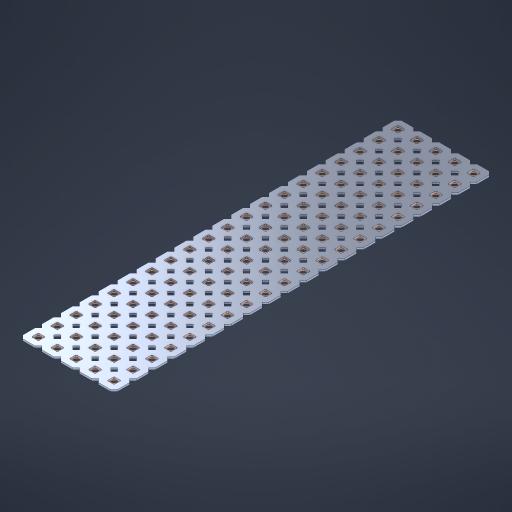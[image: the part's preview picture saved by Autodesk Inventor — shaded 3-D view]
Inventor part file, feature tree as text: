
AUTODESK INVENTOR PART (.ipt)
format: ipt  version: 2023 (Build 270158000, 158)  size: 1,413,120 bytes
history: native  units: in
note: dims shown in document units (in); Inventor stores cm internally (conversion verified against a paired STEP export)
features: other x101, extrude x99, sketch x2, pattern_linear x1
ambient origin geometry x8: Origin, YZ Plane, XZ Plane, XY Plane, X Axis, Y Axis, Z Axis, Center Point
bodies: Solid1 (feature_tree), Body (feature_tree)
feature tree (203):
  pattern_linear  "Rectangular Pattern1"  Spacing1=0.09in  [1 undecoded]
  sketch  "Sketch1"  dims[d1=0.5in]
  sketch  "Sketch2"  dims[d2=0.182in d3=0.09in d4=0.09in d5=0.09in d6=0.09in d7=0.09in d8=0.09in d9=0.09in d10=0.09in d11=0.02in d13=0.0in d14=0.172in d15=0.0625in d16=0.0in d19=0.5in d22=0.5in]
  other  "Srf1"
  other  "Srf126"
  other  "Srf127"
  other  "Srf128"
  other  "Srf129"
  other  "Srf130"
  other  "Srf131"
  other  "Srf250"
  other  "Srf251"
  other  "Srf252"
  other  "Srf253"
  other  "Srf254"
  other  "Srf255"
  other  "Srf256"
  other  "Srf257"
  other  "Srf258"
  other  "Srf259"
  other  "Srf260"
  other  "Srf261"
  other  "Srf262"
  other  "Srf268"
  other  "Srf269"
  other  "Srf270"
  other  "Srf271"
  other  "Srf272"
  other  "Srf273"
  other  "Srf274"
  other  "Srf275"
  other  "Srf276"
  other  "Srf277"
  other  "Srf278"
  other  "Srf279"
  other  "Srf280"
  other  "Srf281"
  other  "Srf282"
  other  "Srf283"
  other  "Srf284"
  other  "Srf285"
  other  "Srf286"
  other  "Srf287"
  other  "Srf293"
  other  "Srf294"
  other  "Srf295"
  other  "Srf296"
  other  "Srf297"
  other  "Srf298"
  other  "Srf299"
  other  "Srf300"
  other  "Srf301"
  other  "Srf302"
  other  "Srf303"
  other  "Srf304"
  other  "Srf305"
  other  "Srf306"
  other  "Srf307"
  other  "Srf308"
  other  "Srf309"
  other  "Srf310"
  other  "Srf311"
  other  "Srf312"
  other  "Srf318"
  other  "Srf319"
  other  "Srf320"
  other  "Srf321"
  other  "Srf322"
  other  "Srf323"
  other  "Srf324"
  other  "Srf325"
  other  "Srf326"
  other  "Srf327"
  other  "Srf328"
  other  "Srf329"
  other  "Srf330"
  other  "Srf331"
  other  "Srf332"
  other  "Srf333"
  other  "Srf334"
  other  "Srf335"
  other  "Srf336"
  other  "Srf337"
  other  "Srf343"
  other  "Srf344"
  other  "Srf345"
  other  "Srf346"
  other  "Srf347"
  other  "Srf348"
  other  "Srf349"
  other  "Srf350"
  other  "Srf351"
  other  "Srf352"
  other  "Srf353"
  other  "Srf354"
  other  "Srf355"
  other  "Srf356"
  other  "Srf357"
  other  "Srf358"
  other  "Srf359"
  other  "Srf360"
  other  "Srf361"
  other  "Srf362"
  other  "Circle"
  extrude  "ExtrusionSrf126"  Depth=0.09in
  extrude  "ExtrusionSrf127"  Depth=0.09in
  extrude  "ExtrusionSrf128"  Depth=0.09in
  extrude  "ExtrusionSrf129"  Depth=0.09in
  extrude  "ExtrusionSrf130"  Depth=0.09in
  extrude  "ExtrusionSrf131"  Depth=0.09in
  extrude  "ExtrusionSrf250"  Depth=0.09in
  extrude  "ExtrusionSrf251"  Depth=0.02in
  extrude  "ExtrusionSrf252"  TaperAngle=0.0deg  [1 undecoded]
  extrude  "ExtrusionSrf253"  Depth=0.5in
  extrude  "ExtrusionSrf254"  Depth=0.5in TaperAngle=0.0deg
  extrude  "ExtrusionSrf255"  Depth=0.5in
  extrude  "ExtrusionSrf256"  Depth=0.5in
  extrude  "ExtrusionSrf257"  [1 undecoded]
  extrude  "ExtrusionSrf258"  [1 undecoded]
  extrude  "ExtrusionSrf259"  [1 undecoded]
  extrude  "ExtrusionSrf260"  [1 undecoded]
  extrude  "ExtrusionSrf261"  [1 undecoded]
  extrude  "ExtrusionSrf262"  [1 undecoded]
  extrude  "ExtrusionSrf268"  [1 undecoded]
  extrude  "ExtrusionSrf269"  [1 undecoded]
  extrude  "ExtrusionSrf270"  [1 undecoded]
  extrude  "ExtrusionSrf271"  [1 undecoded]
  extrude  "ExtrusionSrf272"  [1 undecoded]
  extrude  "ExtrusionSrf273"  [1 undecoded]
  extrude  "ExtrusionSrf274"  [1 undecoded]
  extrude  "ExtrusionSrf275"  [1 undecoded]
  extrude  "ExtrusionSrf276"  [1 undecoded]
  extrude  "ExtrusionSrf277"  [1 undecoded]
  extrude  "ExtrusionSrf278"  [1 undecoded]
  extrude  "ExtrusionSrf279"  [1 undecoded]
  extrude  "ExtrusionSrf280"  [1 undecoded]
  extrude  "ExtrusionSrf281"  [1 undecoded]
  extrude  "ExtrusionSrf282"  [1 undecoded]
  extrude  "ExtrusionSrf283"  [1 undecoded]
  extrude  "ExtrusionSrf284"  [1 undecoded]
  extrude  "ExtrusionSrf285"  [1 undecoded]
  extrude  "ExtrusionSrf286"  [1 undecoded]
  extrude  "ExtrusionSrf287"  [1 undecoded]
  extrude  "ExtrusionSrf293"  [1 undecoded]
  extrude  "ExtrusionSrf294"  [1 undecoded]
  extrude  "ExtrusionSrf295"  [1 undecoded]
  extrude  "ExtrusionSrf296"  [1 undecoded]
  extrude  "ExtrusionSrf297"  [1 undecoded]
  extrude  "ExtrusionSrf298"  [1 undecoded]
  extrude  "ExtrusionSrf299"  [1 undecoded]
  extrude  "ExtrusionSrf300"  [1 undecoded]
  extrude  "ExtrusionSrf301"  [1 undecoded]
  extrude  "ExtrusionSrf302"  [1 undecoded]
  extrude  "ExtrusionSrf303"  [1 undecoded]
  extrude  "ExtrusionSrf304"  [1 undecoded]
  extrude  "ExtrusionSrf305"  [1 undecoded]
  extrude  "ExtrusionSrf306"  [1 undecoded]
  extrude  "ExtrusionSrf307"  [1 undecoded]
  extrude  "ExtrusionSrf308"  [1 undecoded]
  extrude  "ExtrusionSrf309"  [1 undecoded]
  extrude  "ExtrusionSrf310"  [1 undecoded]
  extrude  "ExtrusionSrf311"  [1 undecoded]
  extrude  "ExtrusionSrf312"  [1 undecoded]
  extrude  "ExtrusionSrf318"  [1 undecoded]
  extrude  "ExtrusionSrf319"  [1 undecoded]
  extrude  "ExtrusionSrf320"  [1 undecoded]
  extrude  "ExtrusionSrf321"  [1 undecoded]
  extrude  "ExtrusionSrf322"  [1 undecoded]
  extrude  "ExtrusionSrf323"  [1 undecoded]
  extrude  "ExtrusionSrf324"  [1 undecoded]
  extrude  "ExtrusionSrf325"  [1 undecoded]
  extrude  "ExtrusionSrf326"  [1 undecoded]
  extrude  "ExtrusionSrf327"  [1 undecoded]
  extrude  "ExtrusionSrf328"  [1 undecoded]
  extrude  "ExtrusionSrf329"  [1 undecoded]
  extrude  "ExtrusionSrf330"  [1 undecoded]
  extrude  "ExtrusionSrf331"  [1 undecoded]
  extrude  "ExtrusionSrf332"  [1 undecoded]
  extrude  "ExtrusionSrf333"  [1 undecoded]
  extrude  "ExtrusionSrf334"  [1 undecoded]
  extrude  "ExtrusionSrf335"  [1 undecoded]
  extrude  "ExtrusionSrf336"  [1 undecoded]
  extrude  "ExtrusionSrf337"  [1 undecoded]
  extrude  "ExtrusionSrf343"  [1 undecoded]
  extrude  "ExtrusionSrf344"  [1 undecoded]
  extrude  "ExtrusionSrf345"  [1 undecoded]
  extrude  "ExtrusionSrf346"  [1 undecoded]
  extrude  "ExtrusionSrf347"  [1 undecoded]
  extrude  "ExtrusionSrf348"  [1 undecoded]
  extrude  "ExtrusionSrf349"  [1 undecoded]
  extrude  "ExtrusionSrf350"  [1 undecoded]
  extrude  "ExtrusionSrf351"  [1 undecoded]
  extrude  "ExtrusionSrf352"  [1 undecoded]
  extrude  "ExtrusionSrf353"  [1 undecoded]
  extrude  "ExtrusionSrf354"  [1 undecoded]
  extrude  "ExtrusionSrf355"  [1 undecoded]
  extrude  "ExtrusionSrf356"  [1 undecoded]
  extrude  "ExtrusionSrf357"  [1 undecoded]
  extrude  "ExtrusionSrf358"  [1 undecoded]
  extrude  "ExtrusionSrf359"  [1 undecoded]
  extrude  "ExtrusionSrf360"  [1 undecoded]
  extrude  "ExtrusionSrf361"  [1 undecoded]
  extrude  "ExtrusionSrf362"  [1 undecoded]
note: 88 required parameter values undecoded (feature->parameter linkage not recoverable at this tier; creation-order binding heuristic only, values carry confidence <= 0.55)
